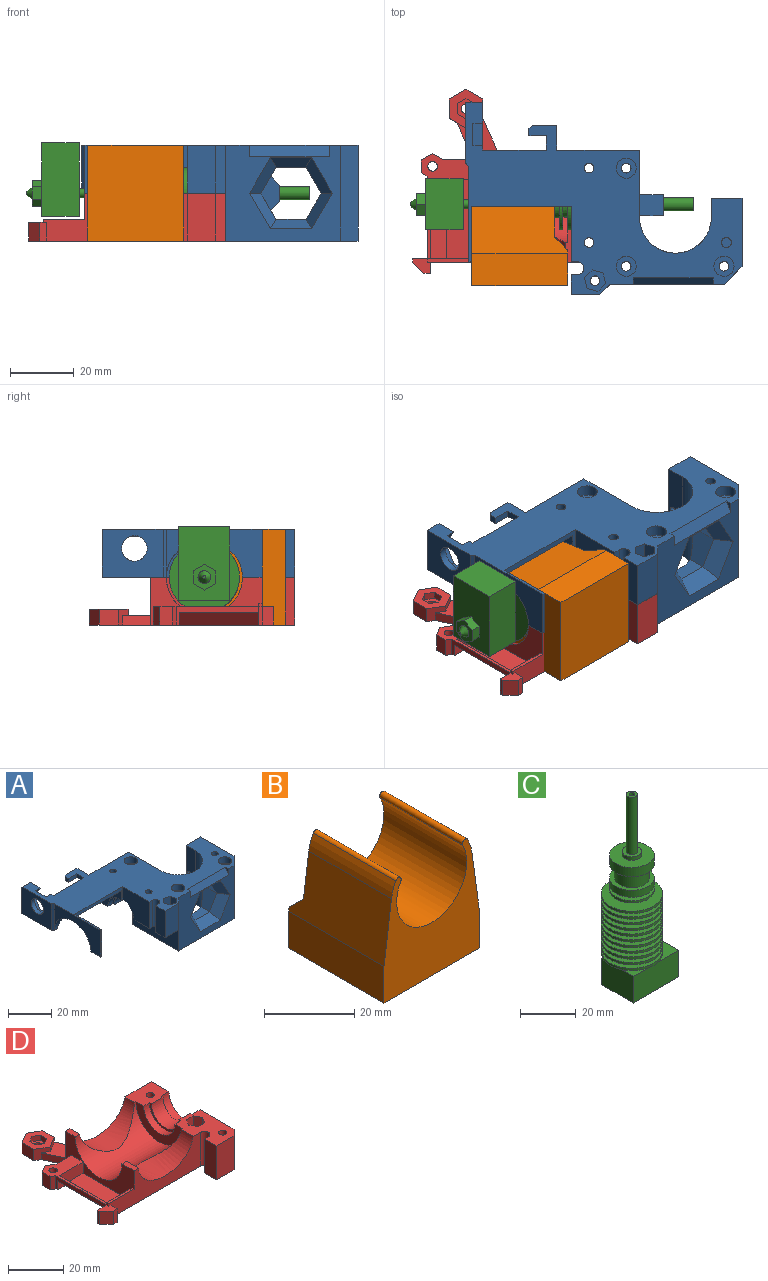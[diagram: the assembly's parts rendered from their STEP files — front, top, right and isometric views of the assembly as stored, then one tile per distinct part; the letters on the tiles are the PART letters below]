
ASSEMBLY  parts=4 mates=3
PART A: 169 faces, bbox 87.6x61.3x31.1 mm
  f0: plane 5.38x3mm, normal (-1,0,0), area 16.2mm2, adj f1,f165,f166,f168
  f1: plane 8.2x5.65mm, normal (0,1,0), area 34.3mm2, adj f0,f2,f5,f162,f163,f164,f165,f168
  f2: plane 8.9x3mm, normal (1,0,0), area 26.7mm2, adj f1,f3,f165,f168
  f3: plane 4x3mm, normal (0,1,0), area 12mm2, adj f2,f4,f165,f168
  f4: plane 3x2.63mm, normal (-1,0,0), area 7.9mm2, adj f3,f165,f166,f168
  f5: plane 8.2x2.5mm, normal (0,0,-1), area 20.5mm2, adj f1,f6,f162,f164
  f6: plane 8.2x5.65mm, normal (0,-1,0), area 34.3mm2, adj f5,f7,f159,f160,f161,f162,f163,f164
  f7: plane 5.6x3mm, normal (1,0,0), area 16.8mm2, adj f6,f8,f159,f161
  f8: plane 30x9.6mm, normal (0,1,0), area 264mm2, adj f7,f9,f20,f21,f22,f23,f155,f158
  f9: plane 5.6x4mm, normal (0,0,1), area 22.4mm2, adj f8,f10,f20,f22
  f10: plane 8.2x5.65mm, normal (0,-1,0), area 34.3mm2, adj f9,f11,f18,f19,f20,f21,f22,f164
  f11: plane 8.2x2.5mm, normal (0,0,1), area 20.5mm2, adj f10,f12,f18,f164
  f12: plane 8.2x5.65mm, normal (0,1,0), area 34.3mm2, adj f11,f13,f15,f16,f17,f18,f19,f164
  f13: plane 8.9x3mm, normal (-1,0,0), area 26.7mm2, adj f12,f14,f15,f17
  f14: plane 4x3mm, normal (0,1,0), area 12mm2, adj f13,f15,f16,f17
  f15: plane 8.9x4mm, normal (0,0,1), area 35.6mm2, adj f12,f13,f14,f16
  f16: plane 8.9x3mm, normal (1,0,0), area 26.7mm2, adj f12,f14,f15,f17
  f17: plane 8.9x4mm, normal (0,0,-1), area 35.6mm2, adj f12,f13,f14,f16
  f18: plane 5.65x2.5mm, normal (1,0,0), area 14.1mm2, adj f10,f11,f12,f19
  f19: plane 8.2x2.5mm, normal (0,0,-1), area 20.5mm2, adj f10,f12,f18,f164
  f20: plane 5.6x3mm, normal (1,0,0), area 16.8mm2, adj f8,f9,f10,f21
  f21: plane 5.6x4mm, normal (0,0,-1), area 22.4mm2, adj f8,f10,f20,f22
  f22: plane 5.6x3mm, normal (-1,0,0), area 16.8mm2, adj f8,f9,f10,f21
  f23: plane 86.5x60.2mm, normal (0,0,1), area 1918.9mm2, adj f8,f24,f94,f95,f96,f97,f99,f100
  f24: plane 25.08x15mm, normal (1,0,0), area 176.8mm2, adj f23,f25,f26,f91,f92,f93,f94,f139
  f25: plane 6.15x0.85mm, normal (0,0,-1), area 5.2mm2, adj f24,f93,f94,f95
  f26: plane 30.15x1.95mm, normal (0,-0.11,-0.99), area 59.2mm2, adj f24,f27,f91,f139
  f27: plane 13.14x12.5mm, normal (-1,0,0), area 70.2mm2, adj f26,f28,f70,f90,f91,f92,f139
  f28: cylinder r=8mm len=16mm, axis (-1,0,0), area 63.4mm2, adj f27,f29,f69,f70,f138,f139
  f29: plane 21.28x11.9mm, normal (0,0,-1), area 189.8mm2, adj f28,f30,f32,f34,f35,f36,f37,f38
  f30: cylinder r=1.5mm len=9mm, axis (0,0,1), area 84.8mm2, adj f29,f31
  f31: plane 6.69x6.69mm, normal (0,0,1), area 24.1mm2, adj f30,f140,f141,f142,f143,f144,f145
  f32: plane 4x3mm, normal (-0.87,0.5,0), area 13.9mm2, adj f29,f33,f34,f38
  f33: plane 6.93x6mm, normal (0,0,-1), area 24.1mm2, adj f32,f34,f35,f36,f37,f38,f153
  f34: plane 4x3.46mm, normal (0,1,0), area 13.9mm2, adj f29,f32,f33,f35
  f35: plane 4x3mm, normal (0.87,0.5,0), area 13.9mm2, adj f29,f33,f34,f36
  f36: plane 4x3mm, normal (0.87,-0.5,0), area 13.9mm2, adj f29,f33,f35,f37
  f37: plane 4x3.46mm, normal (0,-1,0), area 13.9mm2, adj f29,f33,f36,f38
  f38: plane 4x3mm, normal (-0.87,-0.5,0), area 13.9mm2, adj f29,f32,f33,f37
  f39: plane 30.1x23mm, normal (-1,0,0), area 451.3mm2, adj f29,f40,f54,f55,f56,f57,f58,f59
  f40: cylinder r=3.5mm len=4mm, axis (-1,0,0), area 22mm2, adj f39,f41,f54,f60
  f41: plane 13.2x7.4mm, normal (-1,0,0), area 59.1mm2, adj f40,f42,f46,f47,f53,f54,f55,f56
  f42: cylinder r=2mm len=4mm, axis (-1,0,0), area 18.8mm2, adj f41,f43,f45,f46,f53
  f43: cylinder r=3mm len=4mm, axis (0,0,1), area 9.9mm2, adj f42,f44,f45,f46,f53
  f44: bspline ~4.5x3.27mm, area 7.4mm2, adj f43,f46,f47,f53
  f45: cone r=2mm half-angle=45deg, axis (-1,0,0), area 0mm2, adj f42,f43
  f46: plane 4.03x3.55mm, normal (0,1,0), area 11.8mm2, adj f41,f42,f43,f44,f47
  f47: cylinder r=2mm len=13mm, axis (-1,0,0), area 142mm2, adj f41,f44,f46,f48,f53
  f48: plane 6.5x5mm, normal (1,0,0), area 19.9mm2, adj f47,f49,f50,f51,f52
  f49: plane 7.5x7.5mm, normal (0.71,0,0.71), area 68.9mm2, adj f48,f50,f52,f113
  f50: plane 20x7.5mm, normal (0,1,0), area 93.7mm2, adj f48,f49,f51,f113
  f51: plane 7.5x7.5mm, normal (0.71,0,-0.71), area 68.9mm2, adj f48,f50,f52,f113
  f52: plane 20x7.5mm, normal (0,-1,0), area 93.7mm2, adj f48,f49,f51,f113
  f53: plane 4.03x3.56mm, normal (0,-1,0), area 11.8mm2, adj f41,f42,f43,f44,f47
  f54: plane 4x0.4mm, normal (0,0,1), area 1.6mm2, adj f39,f40,f41,f55
  f55: cylinder r=3.5mm len=4mm, axis (1,0,0), area 22mm2, adj f39,f41,f54,f56
  f56: plane 6.2x4mm, normal (0,1,0), area 24.8mm2, adj f39,f41,f55,f57
  f57: cylinder r=3.5mm len=4mm, axis (-1,0,0), area 22mm2, adj f39,f41,f56,f58
  f58: plane 4x0.4mm, normal (0,0,-1), area 1.6mm2, adj f39,f41,f57,f59
  f59: cylinder r=3.5mm len=4mm, axis (1,0,0), area 22mm2, adj f39,f41,f58,f60
  f60: plane 6.2x4mm, normal (0,-1,0), area 24.8mm2, adj f39,f40,f41,f59
  f61: plane 22.5x9.5mm, normal (0,1,0), area 213.7mm2, adj f39,f62,f65,f113,f158
  f62: plane 12x9.5mm, normal (0,0,-1), area 106.9mm2, adj f61,f63,f65,f112,f113
  f63: cylinder r=1.5mm len=4mm, axis (0,0,1), area 37.7mm2, adj f62,f64
  f64: plane 6.3x6.3mm, normal (0,0,1), area 24.1mm2, adj f63,f146
  f65: plane 12x7.5mm, normal (1,0,0), area 76.5mm2, adj f61,f62,f66,f70,f112
  f66: cylinder r=8mm len=16mm, axis (-1,0,0), area 100.5mm2, adj f29,f39,f65,f67,f70
  f67: plane 16x8mm, normal (1,0,0), area 23.6mm2, adj f29,f66,f68,f70
  f68: cylinder r=7mm len=14mm, axis (-1,0,0), area 129.7mm2, adj f29,f67,f69,f70
  f69: plane 16x8mm, normal (-1,0,0), area 23.6mm2, adj f28,f29,f68,f70
  f70: plane 13.65x9.93mm, normal (0,0,-1), area 117.7mm2, adj f27,f28,f65,f66,f67,f68,f69,f71
  f71: extruded ~28x11mm, area 304.7mm2, adj f70,f72,f73,f74,f77,f90,f92,f93
  f72: plane 20x5.25mm, normal (0,0,-1), area 94.5mm2, adj f71,f73,f93,f96,f97,f99,f100
  f73: plane 5.66x2mm, normal (0,-1,0), area 7.7mm2, adj f71,f72,f74,f100
  f74: plane 7.16x6.21mm, normal (0,0.87,0.5), area 27.3mm2, adj f71,f73,f75,f100,f102,f103
  f75: plane 6.93x3mm, normal (0,0,1), area 20.8mm2, adj f74,f76,f100,f102
  f76: plane 6x3.46mm, normal (0,-0.87,0.5), area 20.8mm2, adj f75,f100,f101,f102
  f77: plane 1.34x0.77mm, normal (-1,0,0), area 0.5mm2, adj f71,f103,f112
  f78: cylinder r=1.5mm len=3mm, axis (0,0,-1), area 25.9mm2, adj f70,f79
  f79: plane 8.5x5.6mm, normal (0,0,1), area 40.5mm2, adj f78,f80,f88,f89,f112
  f80: plane 8.5x2.5mm, normal (-1,0,0), area 21.3mm2, adj f79,f81,f88,f112
  f81: plane 8.5x5.6mm, normal (0,0,-1), area 40.5mm2, adj f80,f82,f88,f89,f112
  f82: cylinder r=1.5mm len=3.6mm, axis (0,0,-1), area 33.9mm2, adj f81,f83
  f83: plane 8.5x5.6mm, normal (0,0,1), area 40.5mm2, adj f82,f84,f86,f87,f112
  f84: plane 8.5x2.5mm, normal (-1,0,0), area 21.2mm2, adj f83,f85,f86,f112
  f85: plane 8.5x5.6mm, normal (0,0,-1), area 40.5mm2, adj f84,f86,f87,f112,f154
  f86: plane 5.6x2.5mm, normal (0,1,0), area 14mm2, adj f83,f84,f85,f87
  f87: plane 8.5x2.5mm, normal (1,0,0), area 21.2mm2, adj f83,f85,f86,f112
  f88: plane 5.6x2.5mm, normal (0,1,0), area 14mm2, adj f79,f80,f81,f89
  f89: plane 8.5x2.5mm, normal (1,0,0), area 21.3mm2, adj f79,f81,f88,f112
  f90: extruded ~9.48x7.66mm, area 36mm2, adj f27,f70,f71,f92
  f91: cylinder r=13mm len=30.15mm, axis (-1,0,0), area 163.6mm2, adj f24,f26,f27,f92
  f92: cylinder r=1mm len=30.15mm, axis (-1,0,0), area 48.1mm2, adj f24,f27,f71,f90,f91,f93
  f93: extruded ~23.85x11.25mm, area 74.4mm2, adj f24,f25,f71,f72,f92,f95
  f94: plane 15x0.85mm, normal (0,-1,0), area 12.8mm2, adj f23,f24,f25,f95
  f95: plane 30x15mm, normal (-1,0,0), area 239.3mm2, adj f23,f25,f93,f94,f96
  f96: plane 15x1mm, normal (-0.71,-0.71,0), area 21.2mm2, adj f23,f72,f95,f97
  f97: plane 19x15mm, normal (-1,0,0), area 234.7mm2, adj f23,f72,f96,f98,f99
  f98: cylinder r=4mm len=8mm, axis (-1,0,0), area 56.5mm2, adj f97,f102
  f99: plane 15x5.25mm, normal (0,1,0), area 78.7mm2, adj f23,f72,f97,f100
  f100: plane 15x15mm, normal (1,0,0), area 104.7mm2, adj f23,f72,f73,f74,f75,f76,f99,f101
  f101: plane 6x3.46mm, normal (0,-0.87,-0.5), area 20.8mm2, adj f23,f76,f100,f102
  f102: plane 13.86x12mm, normal (1,0,0), area 74.4mm2, adj f23,f74,f75,f76,f98,f101,f103
  f103: plane 15.57x6.57mm, normal (0,0.87,-0.5), area 54.4mm2, adj f23,f71,f74,f77,f102,f104,f112
  f104: plane 2.66x1.54mm, normal (1,0,0), area 2mm2, adj f23,f103,f112
  f105: plane 4.5x2.1mm, normal (-1,0,0), area 9.4mm2, adj f23,f106,f107,f112
  f106: plane 8.7x7.75mm, normal (0,0,-1), area 42.4mm2, adj f105,f107,f108,f109,f110,f111,f112
  f107: plane 5.45x2.1mm, normal (0,-1,0), area 11.4mm2, adj f23,f105,f106,f108
  f108: plane 2.25x2.1mm, normal (-1,0,0), area 4.7mm2, adj f23,f106,f107,f109
  f109: plane 2.1x1mm, normal (-0.71,0.71,0), area 3mm2, adj f23,f106,f108,f110
  f110: plane 7.7x2.1mm, normal (0,1,0), area 16.2mm2, adj f23,f106,f109,f111
  f111: plane 7.75x2.1mm, normal (1,0,0), area 16.3mm2, adj f23,f106,f110,f112
  f112: plane 49.15x15mm, normal (0,1,0), area 362.1mm2, adj f23,f62,f65,f70,f71,f77,f79,f80
  f113: plane 30x21mm, normal (1,0,0), area 230mm2, adj f23,f49,f50,f51,f52,f61,f62,f112
  f114: cylinder r=11.25mm len=30mm, axis (0,0,1), area 795.5mm2, adj f23,f113,f115,f122,f123,f124,f125,f126
  f115: plane 10.99x9.27mm, normal (0.87,0,-0.5), area 69.8mm2, adj f114,f116,f122,f126
  f116: plane 11.2x8.2mm, normal (0.75,-0.5,-0.43), area 67.2mm2, adj f115,f117,f121,f131
  f117: plane 11.2x8.2mm, normal (0.75,-0.5,0.43), area 67.2mm2, adj f116,f118,f122,f131
  f118: plane 12.93x5.2mm, normal (0,-0.5,0.87), area 67.2mm2, adj f117,f119,f123,f131
  f119: plane 11.2x8.2mm, normal (-0.75,-0.5,0.43), area 67.2mm2, adj f118,f120,f124,f131
  f120: plane 11.2x8.2mm, normal (-0.75,-0.5,-0.43), area 67.2mm2, adj f119,f121,f125,f131
  f121: plane 12.93x5.2mm, normal (0,-0.5,-0.87), area 67.2mm2, adj f116,f120,f126,f131
  f122: plane 10.99x9.27mm, normal (0.87,0,0.5), area 69.8mm2, adj f114,f115,f117,f123
  f123: plane 9.47x5.65mm, normal (0,0,1), area 46.4mm2, adj f114,f118,f122,f124
  f124: plane 10.52x9.18mm, normal (-0.87,0,0.5), area 67.8mm2, adj f114,f119,f123,f125
  f125: plane 10.52x9.18mm, normal (-0.87,0,-0.5), area 67.8mm2, adj f114,f120,f124,f126
  f126: plane 9.47x5.65mm, normal (0,0,-1), area 46.4mm2, adj f114,f115,f121,f125
  f127: plane 30x5.5mm, normal (0.71,-0.71,0), area 233.3mm2, adj f23,f131,f158,f164
  f128: plane 3.46x2mm, normal (-1,0,0), area 3.5mm2, adj f23,f129,f131
  f129: plane 25x3.46mm, normal (0,-0.87,0.5), area 100mm2, adj f23,f128,f130,f131
  f130: plane 3.46x2mm, normal (1,0,0), area 3.5mm2, adj f23,f129,f131
  f131: plane 36x30mm, normal (0,-1,0), area 558.9mm2, adj f23,f116,f117,f118,f119,f120,f121,f127
  f132: plane 30x3.2mm, normal (0.71,-0.71,0), area 70mm2, adj f23,f29,f39,f131,f133,f158
  f133: plane 15x8.8mm, normal (0,-1,0), area 132mm2, adj f23,f29,f132,f134
  f134: plane 15x6.2mm, normal (-1,0,0), area 93mm2, adj f23,f29,f133,f135
  f135: plane 15x2mm, normal (0,1,0), area 30mm2, adj f23,f29,f134,f136
  f136: cylinder r=2mm len=15mm, axis (0,0,1), area 94.2mm2, adj f23,f29,f135,f137
  f137: plane 15x2mm, normal (0,-1,0), area 30mm2, adj f23,f29,f136,f138
  f138: plane 17.5x15mm, normal (-1,0,0), area 216.8mm2, adj f23,f28,f29,f137,f139
  f139: plane 31.15x7.02mm, normal (0,-1,0), area 63.3mm2, adj f23,f24,f26,f27,f28,f138
  f140: plane 6x3.35mm, normal (0.26,0.97,0), area 20.8mm2, adj f23,f31,f141,f145
  f141: plane 6x2.45mm, normal (-0.71,0.71,0), area 20.8mm2, adj f23,f31,f140,f142
  f142: plane 6x3.35mm, normal (-0.97,-0.26,0), area 20.8mm2, adj f23,f31,f141,f143
  f143: plane 6x3.35mm, normal (-0.26,-0.97,0), area 20.8mm2, adj f23,f31,f142,f144
  f144: plane 6x2.45mm, normal (0.71,-0.71,0), area 20.8mm2, adj f23,f31,f143,f145
  f145: plane 6x3.35mm, normal (0.97,0.26,0), area 20.8mm2, adj f23,f31,f140,f144
  f146: cylinder r=3.15mm len=6.3mm, axis (0,0,1), area 69.3mm2, adj f23,f64
  f147: cylinder r=3.15mm len=6.3mm, axis (0,0,1), area 69.3mm2, adj f23,f148
  f148: plane 6.3x6.3mm, normal (0,0,1), area 24.1mm2, adj f147,f149
  f149: cylinder r=1.5mm len=26.5mm, axis (0,0,1), area 249.8mm2, adj f148,f158
  f150: cylinder r=3.15mm len=6.3mm, axis (0,0,1), area 69.3mm2, adj f23,f151
  f151: plane 6.3x6.3mm, normal (0,0,1), area 24.1mm2, adj f150,f152
  f152: cylinder r=1.5mm len=26.5mm, axis (0,0,1), area 249.8mm2, adj f151,f158
  f153: cylinder r=1.5mm len=11mm, axis (0,0,-1), area 103.7mm2, adj f23,f33
  f154: cylinder r=1.5mm len=3.65mm, axis (0,0,-1), area 34.4mm2, adj f23,f85
  f155: plane 30x6mm, normal (-1,0,0), area 175.1mm2, adj f8,f23,f114,f156,f158
  f156: cylinder r=1.25mm len=9.1mm, axis (1,0,0), area 71.5mm2, adj f155,f157
  f157: cone r=1.25mm half-angle=45deg, axis (1,0,0), area 6.7mm2, adj f156,f164
  f158: plane 41.6x30.1mm, normal (0,0,-1), area 788.6mm2, adj f8,f39,f61,f113,f114,f127,f131,f132
  f159: plane 5.6x4mm, normal (0,0,1), area 22.4mm2, adj f6,f7,f8,f160
  f160: plane 5.6x3mm, normal (-1,0,0), area 16.8mm2, adj f6,f8,f159,f161
  f161: plane 5.6x4mm, normal (0,0,-1), area 22.4mm2, adj f6,f7,f8,f160
  f162: plane 5.65x2.5mm, normal (1,0,0), area 14.1mm2, adj f1,f5,f6,f163
  f163: plane 8.2x2.5mm, normal (0,0,1), area 20.5mm2, adj f1,f6,f162,f164
  f164: plane 30x21.5mm, normal (1,0,0), area 607.1mm2, adj f1,f5,f6,f8,f10,f11,f12,f19
  f165: plane 8.9x4mm, normal (0,0,-1), area 28.1mm2, adj f0,f1,f2,f3,f4,f166
  f166: cylinder r=1.55mm len=15mm, axis (0,0,1), area 119.6mm2, adj f0,f4,f23,f165,f167,f168
  f167: plane 3.1x3.1mm, normal (0,0,1), area 7.5mm2, adj f166
  f168: plane 8.9x4mm, normal (0,0,1), area 28.1mm2, adj f0,f1,f2,f3,f4,f166
PART B: 18 faces, bbox 30x30x31.8 mm
  f0: plane 16.41x9.64mm, normal (0,1,0), area 54.9mm2, adj f1,f2,f3,f4,f16
  f1: cylinder r=11mm len=26.6mm, axis (0,1,0), area 1179.5mm2, adj f0,f2,f10,f11,f12,f14,f15,f16
  f2: cylinder r=0.88mm len=26mm, axis (0,1,0), area 71.5mm2, adj f0,f1,f3,f11
  f3: cylinder r=12.75mm len=26mm, axis (0,1,0), area 115.6mm2, adj f0,f2,f4,f11
  f4: plane 30.01x17.15mm, normal (-0.99,0,0.14), area 462.1mm2, adj f0,f3,f5,f11,f13,f14,f16,f17
  f5: plane 30x10mm, normal (-1,0,0), area 300mm2, adj f4,f6,f11,f13
  f6: plane 30x30mm, normal (0,0,-1), area 900mm2, adj f5,f7,f11,f13
  f7: plane 30x10mm, normal (1,0,0), area 300mm2, adj f6,f8,f11,f13
  f8: plane 30.01x17.15mm, normal (0.99,0,0.14), area 462.1mm2, adj f7,f9,f11,f12,f13,f14,f15,f17
  f9: cylinder r=12.75mm len=26mm, axis (0,1,0), area 115.6mm2, adj f8,f10,f11,f12
  f10: cylinder r=0.88mm len=26mm, axis (0,1,0), area 71.5mm2, adj f1,f9,f11,f12
  f11: plane 31.82x30mm, normal (0,-1,0), area 561.9mm2, adj f1,f2,f3,f4,f5,f6,f7,f8
  f12: plane 16.41x9.64mm, normal (0,1,0), area 54.9mm2, adj f1,f8,f9,f10,f15
  f13: plane 30x10.59mm, normal (0,1,0), area 317.5mm2, adj f4,f5,f6,f7,f8,f17
  f14: plane 29.64x3.41mm, normal (0,0.71,0.71), area 139.3mm2, adj f1,f4,f8,f15,f16,f17
  f15: cylinder r=1mm len=11.77mm, axis (1,0,0), area 8.4mm2, adj f1,f8,f12,f14
  f16: cylinder r=1mm len=11.77mm, axis (1,0,0), area 8.4mm2, adj f0,f1,f4,f14
  f17: cylinder r=1mm len=29.84mm, axis (-1,0,0), area 23.4mm2, adj f4,f8,f13,f14
PART C: 77 faces, bbox 26.8x22x88.9 mm
  f0: plane 1x1mm, normal (0,0,-1), area 0.8mm2, adj f1
  f1: cone r=0.5mm half-angle=36.9deg, axis (0,0,1), area 19.6mm2, adj f0,f8
  f2: plane 4.04x3mm, normal (0,-1,0), area 12.1mm2, adj f3,f7,f8,f9
  f3: plane 3.5x3mm, normal (0.87,-0.5,0), area 12.1mm2, adj f2,f4,f8,f9
  f4: plane 3.5x3mm, normal (0.87,0.5,0), area 12.1mm2, adj f3,f5,f8,f9
  f5: plane 4.04x3mm, normal (0,1,0), area 12.1mm2, adj f4,f6,f8,f9
  f6: plane 3.5x3mm, normal (-0.87,0.5,0), area 12.1mm2, adj f5,f7,f8,f9
  f7: plane 3.5x3mm, normal (-0.87,-0.5,0), area 12.1mm2, adj f2,f6,f8,f9
  f8: plane 8.08x7mm, normal (0,0,-1), area 29.9mm2, adj f1,f2,f3,f4,f5,f6,f7
  f9: plane 23x16mm, normal (0,0,-1), area 325.6mm2, adj f2,f3,f4,f5,f6,f7,f10,f11
  f10: plane 23x11.6mm, normal (0,-1,0), area 266.8mm2, adj f9,f11,f13,f14
  f11: plane 16x11.6mm, normal (1,0,0), area 185.6mm2, adj f9,f10,f12,f14
  f12: plane 23x11.6mm, normal (0,1,0), area 266.8mm2, adj f9,f11,f13,f14
  f13: plane 16x11.6mm, normal (-1,0,0), area 185.6mm2, adj f9,f10,f12,f14
  f14: plane 23x16mm, normal (0,0,1), area 362.1mm2, adj f10,f11,f12,f13,f15
  f15: cylinder r=1.38mm len=2.75mm, axis (0,0,-1), area 23.8mm2, adj f14,f16
  f16: plane 22x22mm, normal (0,0,-1), area 374.2mm2, adj f15,f17
  f17: cylinder r=11mm len=22mm, axis (0,0,-1), area 69.1mm2, adj f16,f18
  f18: plane 22x22mm, normal (0,0,1), area 267mm2, adj f17,f19
  f19: cone r=6mm half-angle=4deg, axis (0,0,-1), area 56.2mm2, adj f18,f20
  f20: plane 22x22mm, normal (0,0,-1), area 270.9mm2, adj f19,f21
  f21: cylinder r=11mm len=22mm, axis (0,0,-1), area 69.1mm2, adj f20,f22
  f22: plane 22x22mm, normal (0,0,1), area 273.5mm2, adj f21,f23
  f23: cone r=5.83mm half-angle=4deg, axis (0,0,-1), area 54.6mm2, adj f22,f24
  f24: plane 22x22mm, normal (0,0,-1), area 277.2mm2, adj f23,f25
  f25: cylinder r=11mm len=22mm, axis (0,0,-1), area 69.1mm2, adj f24,f26
  f26: plane 22x22mm, normal (0,0,1), area 279.7mm2, adj f25,f27
  f27: cone r=5.65mm half-angle=4deg, axis (0,0,-1), area 52.9mm2, adj f26,f28
  f28: plane 22x22mm, normal (0,0,-1), area 283.3mm2, adj f27,f29
  f29: cylinder r=11mm len=22mm, axis (0,0,-1), area 69.1mm2, adj f28,f30
  f30: plane 22x22mm, normal (0,0,1), area 285.7mm2, adj f29,f31
  f31: cone r=5.48mm half-angle=4deg, axis (0,0,-1), area 51.3mm2, adj f30,f32
  f32: plane 22x22mm, normal (0,0,-1), area 289.3mm2, adj f31,f33
  f33: cylinder r=11mm len=22mm, axis (0,0,-1), area 69.1mm2, adj f32,f34
  f34: plane 22x22mm, normal (0,0,1), area 291.6mm2, adj f33,f35
  f35: cone r=5.31mm half-angle=4deg, axis (0,0,-1), area 49.7mm2, adj f34,f36
  f36: plane 22x22mm, normal (0,0,-1), area 295mm2, adj f35,f37
  f37: cylinder r=11mm len=22mm, axis (0,0,-1), area 69.1mm2, adj f36,f38
  f38: plane 22x22mm, normal (0,0,1), area 297.3mm2, adj f37,f39
  f39: cone r=5.14mm half-angle=4deg, axis (0,0,-1), area 48mm2, adj f38,f40
  f40: plane 22x22mm, normal (0,0,-1), area 300.6mm2, adj f39,f41
  f41: cylinder r=11mm len=22mm, axis (0,0,-1), area 69.1mm2, adj f40,f42
  f42: plane 22x22mm, normal (0,0,1), area 302.8mm2, adj f41,f43
  f43: cone r=4.96mm half-angle=4deg, axis (0,0,-1), area 46.4mm2, adj f42,f44
  f44: plane 22x22mm, normal (0,0,-1), area 306mm2, adj f43,f45
  f45: cylinder r=11mm len=22mm, axis (0,0,-1), area 69.1mm2, adj f44,f46
  f46: plane 22x22mm, normal (0,0,1), area 308.1mm2, adj f45,f47
  f47: cone r=4.79mm half-angle=4deg, axis (0,0,-1), area 44.8mm2, adj f46,f48
  f48: plane 22x22mm, normal (0,0,-1), area 311.2mm2, adj f47,f49
  f49: cylinder r=11mm len=22mm, axis (0,0,-1), area 69.1mm2, adj f48,f50
  f50: plane 22x22mm, normal (0,0,1), area 313.2mm2, adj f49,f51
  f51: cone r=4.62mm half-angle=4deg, axis (0,0,-1), area 43.1mm2, adj f50,f52
  f52: plane 22x22mm, normal (0,0,-1), area 316.1mm2, adj f51,f53
  f53: cylinder r=11mm len=22mm, axis (0,0,-1), area 69.1mm2, adj f52,f54
  f54: plane 22x22mm, normal (0,0,1), area 318.1mm2, adj f53,f55
  f55: cone r=4.44mm half-angle=4deg, axis (0,0,-1), area 41.5mm2, adj f54,f56
  f56: plane 22x22mm, normal (0,0,-1), area 321mm2, adj f55,f57
  f57: cylinder r=11mm len=22mm, axis (0,0,-1), area 69.1mm2, adj f56,f58
  f58: plane 22x22mm, normal (0,0,1), area 322.8mm2, adj f57,f59
  f59: cone r=4.27mm half-angle=4deg, axis (0,0,-1), area 39.9mm2, adj f58,f60
  f60: plane 16x16mm, normal (0,0,-1), area 146.5mm2, adj f59,f61
  f61: cylinder r=8mm len=16mm, axis (0,0,-1), area 50.3mm2, adj f60,f62
  f62: plane 16x16mm, normal (0,0,1), area 148.3mm2, adj f61,f63
  f63: cone r=4.1mm half-angle=4deg, axis (0,0,-1), area 38.2mm2, adj f62,f64
  f64: plane 16x16mm, normal (0,0,-1), area 150.9mm2, adj f63,f65
  f65: cylinder r=8mm len=16mm, axis (0,0,-1), area 150.8mm2, adj f64,f66
  f66: plane 16x16mm, normal (0,0,1), area 78.3mm2, adj f65,f67
  f67: cylinder r=6.25mm len=12.5mm, axis (0,0,-1), area 235.6mm2, adj f66,f68
  f68: plane 16x16mm, normal (0,0,-1), area 78.3mm2, adj f67,f69
  f69: cylinder r=8mm len=16mm, axis (0,0,-1), area 201.1mm2, adj f68,f70
  f70: plane 16x16mm, normal (0,0,1), area 162.6mm2, adj f69,f71
  f71: cylinder r=3.5mm len=7mm, axis (0,0,-1), area 33mm2, adj f70,f72
  f72: plane 7x7mm, normal (0,0,1), area 25.9mm2, adj f71,f74
  f73: cylinder r=1mm len=25mm, axis (0,0,-1), area 157.1mm2, adj f75,f76
  f74: cylinder r=2mm len=25mm, axis (0,0,-1), area 314.2mm2, adj f72,f75
  f75: plane 4x4mm, normal (0,0,1), area 9.4mm2, adj f73,f74
  f76: plane 2x2mm, normal (0,0,1), area 3.1mm2, adj f73
PART D: 77 faces, bbox 61.5x64.3x15 mm
  f0: plane 7.85x5.85mm, normal (0,1,0), area 45.9mm2, adj f7,f11,f23,f76
  f1: plane 13.1x6mm, normal (0,1,0), area 61.1mm2, adj f7,f66,f67,f69,f70,f76
  f2: plane 13.65x9.93mm, normal (0,0,1), area 117.7mm2, adj f4,f21,f25,f50,f51,f52,f53,f54
  f3: plane 21.28x13.65mm, normal (0,0,1), area 204.8mm2, adj f10,f22,f24,f25,f26,f27,f28,f47
  f4: plane 43.9x15mm, normal (0,1,0), area 411.6mm2, adj f2,f5,f23,f25,f29,f30,f37,f74
  f5: plane 5x2.25mm, normal (0,0,1), area 11.2mm2, adj f4,f73,f74,f76
  f6: plane 25x4mm, normal (-0.71,0,-0.71), area 141.4mm2, adj f9,f15,f23,f71
  f7: plane 33.02x14.85mm, normal (0,0,1), area 111.6mm2, adj f0,f1,f9,f11,f12,f13,f14,f20
  f8: plane 6.15x2.25mm, normal (0,0,1), area 13.8mm2, adj f10,f73,f75,f76
  f9: plane 25.95x5.85mm, normal (-1,0,0), area 51.8mm2, adj f6,f7,f14,f15,f23,f71
  f10: plane 47.1x15mm, normal (0,-1,0), area 373.2mm2, adj f3,f8,f19,f23,f28,f65,f66,f67
  f11: plane 5.85x3.5mm, normal (0.5,0.87,0), area 23.6mm2, adj f0,f7,f12,f23
  f12: plane 5.85x3.5mm, normal (-0.5,0.87,0), area 23.6mm2, adj f7,f11,f13,f23
  f13: plane 5.85x4.04mm, normal (-1,0,0), area 23.6mm2, adj f7,f12,f14,f23
  f14: plane 5.85x1.75mm, normal (-0.5,-0.87,0), area 11.8mm2, adj f7,f9,f13,f23
  f15: plane 8.5x5.85mm, normal (0,1,0), area 34.3mm2, adj f6,f9,f16,f23,f65
  f16: plane 5.85x1mm, normal (-1,0,0), area 5.8mm2, adj f15,f17,f23,f65
  f17: plane 5.85x3.5mm, normal (-0.71,-0.71,0), area 29mm2, adj f16,f18,f23,f65
  f18: plane 5.85x2mm, normal (0,-1,0), area 11.7mm2, adj f17,f19,f23,f65
  f19: plane 5.85x3.5mm, normal (1,0,0), area 20.5mm2, adj f10,f18,f23,f65
  f20: cylinder r=1.5mm len=5.85mm, axis (0,0,1), area 55.1mm2, adj f7,f23
  f21: cylinder r=1.5mm len=11.5mm, axis (0,0,1), area 108.4mm2, adj f2,f55
  f22: cylinder r=1.5mm len=11.5mm, axis (0,0,1), area 108.4mm2, adj f3,f48
  f23: plane 64.29x61.5mm, normal (0,0,-1), area 2081.5mm2, adj f0,f4,f6,f9,f10,f11,f12,f13
  f24: plane 15x6.2mm, normal (-1,0,0), area 93mm2, adj f3,f23,f26,f27
  f25: plane 42.2x15mm, normal (1,0,0), area 532.5mm2, adj f2,f3,f4,f23,f47,f51
  f26: plane 15x8.9mm, normal (0,-1,0), area 133.5mm2, adj f3,f23,f24,f47
  f27: plane 15x2mm, normal (0,1,0), area 30mm2, adj f3,f23,f24,f28
  f28: cylinder r=2mm len=15mm, axis (0,0,1), area 94.2mm2, adj f3,f10,f23,f27
  f29: plane 8.63x3.95mm, normal (-0.91,-0.42,0), area 28.5mm2, adj f4,f23,f35,f37
  f30: plane 10x4.58mm, normal (0.91,0.42,0), area 33mm2, adj f4,f23,f31,f37
  f31: plane 6.06x5mm, normal (1,0,0), area 30.3mm2, adj f23,f30,f32,f36,f38
  f32: plane 5.25x5mm, normal (0.5,0.87,0), area 30.3mm2, adj f23,f31,f33,f38
  f33: plane 5.25x5mm, normal (-0.5,0.87,0), area 30.3mm2, adj f23,f32,f34,f38
  f34: plane 6.06x5mm, normal (-1,0,0), area 30.3mm2, adj f23,f33,f35,f38
  f35: plane 5.25x5mm, normal (-0.5,-0.87,0), area 20.4mm2, adj f23,f29,f34,f36,f37,f38
  f36: plane 5.25x3.03mm, normal (0.5,-0.87,0), area 12.1mm2, adj f31,f35,f37,f38
  f37: plane 12.7x10mm, normal (0,0,1), area 72.8mm2, adj f4,f29,f30,f35,f36
  f38: plane 12.12x10.5mm, normal (0,0,1), area 69.3mm2, adj f31,f32,f33,f34,f35,f36,f39,f40
  f39: plane 3.18x2.25mm, normal (1,0,0), area 7.1mm2, adj f38,f40,f44,f45
  f40: plane 2.75x2.25mm, normal (0.5,0.87,0), area 7.1mm2, adj f38,f39,f41,f45
  f41: plane 2.75x2.25mm, normal (-0.5,0.87,0), area 7.1mm2, adj f38,f40,f42,f45
  f42: plane 3.18x2.25mm, normal (-1,0,0), area 7.1mm2, adj f38,f41,f43,f45
  f43: plane 2.75x2.25mm, normal (-0.5,-0.87,0), area 7.1mm2, adj f38,f42,f44,f45
  f44: plane 2.75x2.25mm, normal (0.5,-0.87,0), area 7.1mm2, adj f38,f39,f43,f45
  f45: plane 6.35x5.5mm, normal (0,0,1), area 19.1mm2, adj f39,f40,f41,f42,f43,f44,f46
  f46: cylinder r=1.5mm len=3mm, axis (0,0,1), area 25.9mm2, adj f23,f45
  f47: plane 15x3mm, normal (0.71,-0.71,0), area 63.6mm2, adj f3,f23,f25,f26
  f48: plane 6x6mm, normal (0,0,-1), area 21.2mm2, adj f22,f49
  f49: cylinder r=3mm len=6mm, axis (0,0,-1), area 66mm2, adj f23,f48
  f50: plane 16x8mm, normal (1,0,0), area 23.6mm2, adj f2,f3,f51,f52
  f51: cylinder r=8mm len=16mm, axis (1,0,0), area 100.5mm2, adj f2,f3,f25,f50
  f52: cylinder r=7mm len=14mm, axis (-1,0,0), area 129.7mm2, adj f2,f3,f50,f53
  f53: plane 16x8mm, normal (-1,0,0), area 23.6mm2, adj f2,f3,f52,f54
  f54: cylinder r=8mm len=16mm, axis (-1,0,0), area 75.4mm2, adj f2,f3,f53,f72
  f55: plane 6x6mm, normal (0,0,-1), area 21.2mm2, adj f21,f56
  f56: cylinder r=3mm len=6mm, axis (0,0,-1), area 66mm2, adj f23,f55
  f57: plane 13.2x3.46mm, normal (0,1,0), area 45.7mm2, adj f3,f58,f62,f63
  f58: plane 13.2x3mm, normal (-0.87,0.5,0), area 45.7mm2, adj f3,f57,f59,f63
  f59: plane 13.2x3mm, normal (-0.87,-0.5,0), area 45.7mm2, adj f3,f58,f60,f63
  f60: plane 13.2x3.46mm, normal (0,-1,0), area 45.7mm2, adj f3,f59,f61,f63
  f61: plane 13.2x3mm, normal (0.87,-0.5,0), area 45.7mm2, adj f3,f60,f62,f63
  f62: plane 13.2x3mm, normal (0.87,0.5,0), area 45.7mm2, adj f3,f57,f61,f63
  f63: plane 6.93x6mm, normal (0,0,1), area 24.1mm2, adj f57,f58,f59,f60,f61,f62,f64
  f64: cylinder r=1.5mm len=3mm, axis (0,0,1), area 17mm2, adj f23,f63
  f65: plane 5.5x4.5mm, normal (0,0,1), area 17.6mm2, adj f10,f15,f16,f17,f18,f19,f66
  f66: plane 1x1mm, normal (-1,0,0), area 1mm2, adj f1,f10,f65,f67
  f67: plane 13.1x1mm, normal (0,0,1), area 13.1mm2, adj f1,f10,f66,f76
  f68: plane 12.1x5mm, normal (0,-1,0), area 48mm2, adj f7,f69,f70,f76
  f69: plane 25x7.1mm, normal (0,0,1), area 177.5mm2, adj f1,f68,f70,f76
  f70: plane 25x5mm, normal (0.71,0,0.71), area 176.8mm2, adj f1,f7,f68,f69
  f71: plane 4x4mm, normal (0,-1,0), area 8mm2, adj f6,f9,f23
  f72: plane 23.85x11.93mm, normal (-1,0,0), area 122.8mm2, adj f2,f3,f54,f73
  f73: cylinder r=11.93mm len=31mm, axis (-1,0,0), area 660.7mm2, adj f2,f3,f5,f8,f72,f74,f75,f76
  f74: extruded ~28x10.79mm, area 297.3mm2, adj f2,f4,f5,f73
  f75: extruded ~28x11.94mm, area 340.9mm2, adj f3,f8,f10,f73
  f76: plane 35x15mm, normal (-1,0,0), area 238.4mm2, adj f0,f1,f4,f5,f7,f8,f10,f23
PLACE A t=(62.82,-4.69,-23.63)mm
PLACE B rot(axis=(-0.58,-0.58,-0.58),120deg) t=(46.97,-5.02,-8.63)mm
PLACE C rot(axis=(-0.71,0,-0.71),180deg) t=(1.62,20.38,-8.63)mm
PLACE D t=(35.47,14.71,-23.63)mm
MATE fastened B.f1 <-> C.f17  axis (1,0,0) through (46.97,20.38,-8.63)mm
MATE fastened D.f22 <-> A.f30  axis (0,0,1) through (59.56,-3.54,-8.63)mm
MATE fastened C.f17 <-> A.f28  axis (1,0,0) through (63.97,20.38,-8.63)mm
